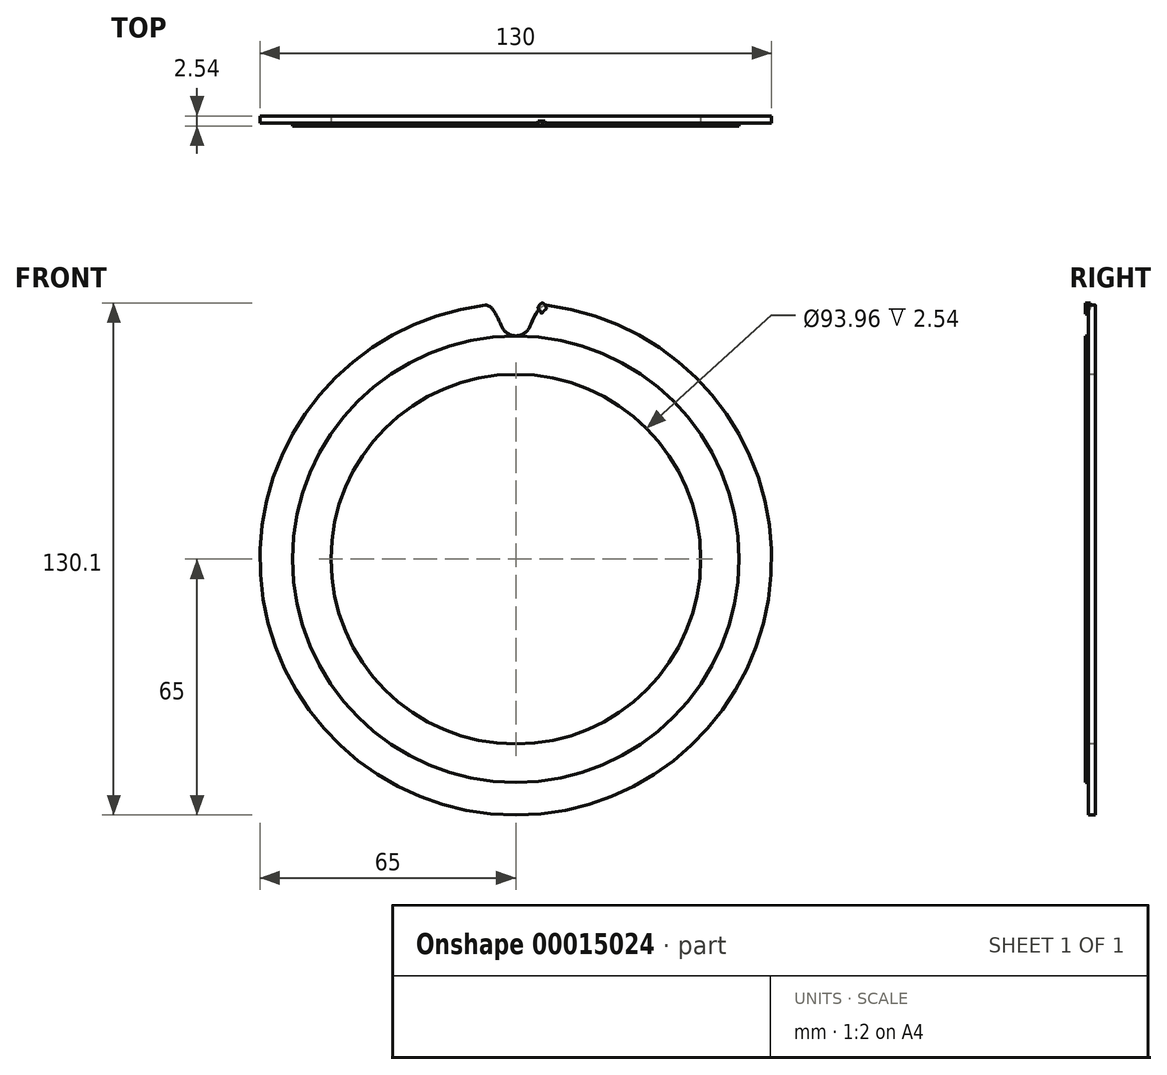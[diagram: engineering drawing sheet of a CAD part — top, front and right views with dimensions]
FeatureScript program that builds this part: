
annotation { "Feature Type Name" : "Feature", "Feature Type Description" : "" }
export const myFeature = defineFeature(function(context is Context, id is Id, definition is map)
    precondition{}
    {
        {
            var Q0;
            Q0=qCreatedBy(makeId("Front.planeOp"),FACE);
            var sketch = newSketch(context, id + "F0", { "sketchPlane" : qUnion([Q0])});
            skCircle(sketch, "E0", {"center": v(0, 0) * mm, "radius": 65 * mm});
            skSolve(sketch);
        }
        {
            var Q0;
            Q0 = qSketchRegion(id + "F0", true);
            extrude(context, id + "F1", {"entities" : qUnion([Q0]), "endBound" : BoundingType.SYMMETRIC, "depth" : 2.54 * mm, "offsetDistance" : 25.4 * mm});
        }
        {
            var Q0;
            Q0=qCreatedBy(makeId("Front.planeOp"),FACE);
            var sketch = newSketch(context, id + "F2", { "sketchPlane" : qUnion([Q0])});
            skCircle(sketch, "E1", {"center": v(0, 0) * mm, "radius": 46.98 * mm});
            skSolve(sketch);
        }
        {
            var Q0;
            Q0 = qSketchRegion(id + "F2", true);
            extrude(context, id + "F3", {"entities" : qUnion([Q0]), "operationType" : NewBodyOperationType.REMOVE, "endBound" : BoundingType.SYMMETRIC, "oppositeDirection" : true, "offsetDistance" : 25.4 * mm, "depth" : 10.6 * mm, "hasSecondDirection" : true, "secondDirectionBound" : SecondDirectionBoundingType.THROUGH_ALL, "secondDirectionOppositeDirection" : false, "secondDirectionDepth" : 25.4 * mm});
        }
        {
            var Q0;
            Q0=qCreatedBy(makeId("Front.planeOp"),FACE);
            var sketch = newSketch(context, id + "F4", { "sketchPlane" : qUnion([Q0])});
            skArc(sketch, "E2", {"start": v(-3.17, 58.35) * mm, "mid": v(0, 56.75) * mm, "end": v(3.17, 58.35) * mm});
            skFitSpline(sketch, "E3", {"points": [v(-3.18, 58.35) * mm, v(-7.73, 64.54) * mm], "startDerivative": vector(-2.09, 2.83) * mm, "endDerivative": vector(-6.83, -0.82) * mm});
            skLineSegment(sketch, "E4", {"start": v(-3.18, 58.35) * mm, "end": v(3.18, 58.35) * mm, "construction": true});
            skLineSegment(sketch, "E5", {"start": v(-3.17, 58.35) * mm, "end": v(-7.73, 64.54) * mm, "construction": true});
            skArc(sketch, "E6", {"start": v(7.73, 64.54) * mm, "mid": v(0, 65) * mm, "end": v(-7.73, 64.54) * mm});
            skFitSpline(sketch, "E7.MirrorCS", {"points": [v(3.18, 58.35) * mm, v(7.73, 64.54) * mm], "startDerivative": vector(2.09, 2.83) * mm, "endDerivative": vector(6.83, -0.82) * mm});
            skLineSegment(sketch, "E8", {"start": v(-31.7, 56.75) * mm, "end": v(31.7, 56.75) * mm, "construction": true});
            skPoint(sketch, "E9", {"position": v(-5.45, 61.45) * mm});
            skSolve(sketch);
        }
        {
            var Q0;
            Q0 = qSketchRegion(id + "F4", true);
            extrude(context, id + "F5", {"entities" : qUnion([Q0]), "operationType" : NewBodyOperationType.REMOVE, "endBound" : BoundingType.THROUGH_ALL, "oppositeDirection" : true, "depth" : 25.4 * mm, "hasSecondDirection" : true, "secondDirectionBound" : SecondDirectionBoundingType.THROUGH_ALL, "secondDirectionOppositeDirection" : false, "secondDirectionDepth" : 25.4 * mm});
        }
        {
            var Q0;
            Q0=qCreatedBy(makeId("Front.planeOp"),FACE);
            var sketch = newSketch(context, id + "F6", { "sketchPlane" : qUnion([Q0])});
            skCircle(sketch, "E10", {"center": v(0, 0) * mm, "radius": 65 * mm, "construction": true});
            skSolve(sketch);
        }
        {
            var Q0;
            Q0=makeQuery(id+"F1.opExtrude","CAP_FACE",FACE,{"disambiguationData":[OSD([sQuery(id+"F0.wireOp",EDGE,"E0")])],"isStart":false});
            var sketch = newSketch(context, id + "F7", { "sketchPlane" : qUnion([Q0])});
            skCircle(sketch, "E11", {"center": v(0, 0) * mm, "radius": 56.75 * mm});
            skCircle(sketch, "E12", {"center": v(0, 0) * mm, "radius": 65 * mm});
            skSolve(sketch);
        }
        {
            var Q0;
            Q0 = qSketchRegion(id + "F7", true);
            extrude(context, id + "F8", {"entities" : qUnion([Q0]), "operationType" : NewBodyOperationType.REMOVE, "oppositeDirection" : true, "offsetDistance" : 25.4 * mm, "depth" : 0.76 * mm});
        }
        {
            var Q0;
            Q0=qCreatedBy(makeId("Front.planeOp"),FACE);
            var sketch = newSketch(context, id + "F9", { "sketchPlane" : qUnion([Q0])});
            skArc(sketch, "E13.0", {"start": v(9.03, 57.74) * mm, "mid": v(10.15, 56.3) * mm, "end": v(11.8, 55.5) * mm});
            skFitSpline(sketch, "E13.1", {"points": [v(8.67, 56.06) * mm, v(8.15, 57.12) * mm, v(7.4, 64.65) * mm, v(4.35, 64.85) * mm]});
            skArc(sketch, "E13.2", {"start": v(3.17, 58.35) * mm, "mid": v(1.78, 57.17) * mm, "end": v(0, 56.75) * mm});
            skFitSpline(sketch, "E13.3", {"points": [v(9.23, 64.34) * mm, v(6.2, 64.78) * mm, v(3.9, 57.56) * mm, v(3.18, 56.64) * mm]});
            skArc(sketch, "E14.0", {"start": v(3.45, 58.15) * mm, "mid": v(1.93, 56.87) * mm, "end": v(0, 56.41) * mm});
            skFitSpline(sketch, "E14.1", {"points": [v(9.18, 64) * mm, v(9.02, 64.03) * mm, v(8.72, 64.03) * mm, v(8.11, 63.84) * mm, v(7.33, 63.28) * mm, v(6.44, 62.19) * mm, v(5.62, 60.85) * mm, v(4.9, 59.44) * mm, v(4.39, 58.33) * mm, v(4.04, 57.58) * mm, v(3.82, 57.1) * mm, v(3.62, 56.7) * mm, v(3.5, 56.52) * mm, v(3.44, 56.43) * mm]});
            skFitSpline(sketch, "E14.2", {"points": [v(8.37, 55.92) * mm, v(8.32, 56.01) * mm, v(8.25, 56.22) * mm, v(8.14, 56.64) * mm, v(8.02, 57.16) * mm, v(7.84, 57.97) * mm, v(7.57, 59.15) * mm, v(7.16, 60.69) * mm, v(6.63, 62.16) * mm, v(5.98, 63.42) * mm, v(5.34, 64.13) * mm, v(4.78, 64.44) * mm, v(4.49, 64.5) * mm, v(4.33, 64.52) * mm]});
            skArc(sketch, "E14.3", {"start": v(8.72, 57.6) * mm, "mid": v(9.94, 56.03) * mm, "end": v(11.73, 55.18) * mm});
            skLineSegment(sketch, "E15", {"start": v(0, 56.41) * mm, "end": v(11.73, 55.18) * mm});
            skSolve(sketch);
        }
        {
            var Q0;
            Q0 = qSketchRegion(id + "F9", true);
            extrude(context, id + "F10", {"entities" : qUnion([Q0]), "operationType" : NewBodyOperationType.ADD, "depth" : 1.22 * mm, "offsetDistance" : 25.4 * mm});
        }
    });
